# Revit family: AFX-Barlow_Vanity-
name_source: partatom
category: Lighting Fixtures
units: mm (PartAtom-declared; Revit-internal decimal feet)

## family parameters
Cut with Voids When Loaded = No
Host = Face
Light Source = Yes
Part Type = Normal
Room Calculation Point = No
Round Connector Dimension = Use Diameter
Shared = No

## types (2) — shared parameters
Apparent Load = 0 VA
Assembly Code = D5020200
Cap Finish = AFX - Black Steel
Color Filter = 16777215
Colour Rendering Index = 90
Cover Plate Finish = AFX - Black Steel
Default Elevation = 48"
Depth = 2 1/4"
Diffuser Finish = AFX - White Acrylic
Dimming Lamp Color Temperature Shift = <None>
Frame Finish = AFX - Black Steel
Height = 4"
Housing Finish = AFX - Black Steel
Keynote = 12500
LED Finish = AFX - White Plastic
Manufacturer = AFX Inc
Product Documentation Link = https://www.afxinc.com
Revit File Built By = https://servex-us.com
Tilt Angle = 0.00°
Type Comments = Barlow
URL = https://www.afxinc.com
Voltage = 120 V
Wattage Comments = 20

## per-type parameters (varying)
| type | Description | Length | Photometric Web File |
| BARV1803L30D1BK | Decorative vanity with a frosted acrylic diffuser with vertical or horizontal mounting - 18"L x 2 1/4"D x 4"H | 18" | BARV1803L30D1xx_IES.IES |
| BARV2403L30D1BK | Decorative vanity with a frosted acrylic diffuser with vertical or horizontal mounting - 24"L x 2 1/4"D x 4"H | 24" | BARV2403L30D1xx_IES 753LM.IES |

note: column(s) folded — value = type name in every type: Model

## geometry (parser evidence)
native form markers: Sweep x2
no freeform markers — native parametric forms only
